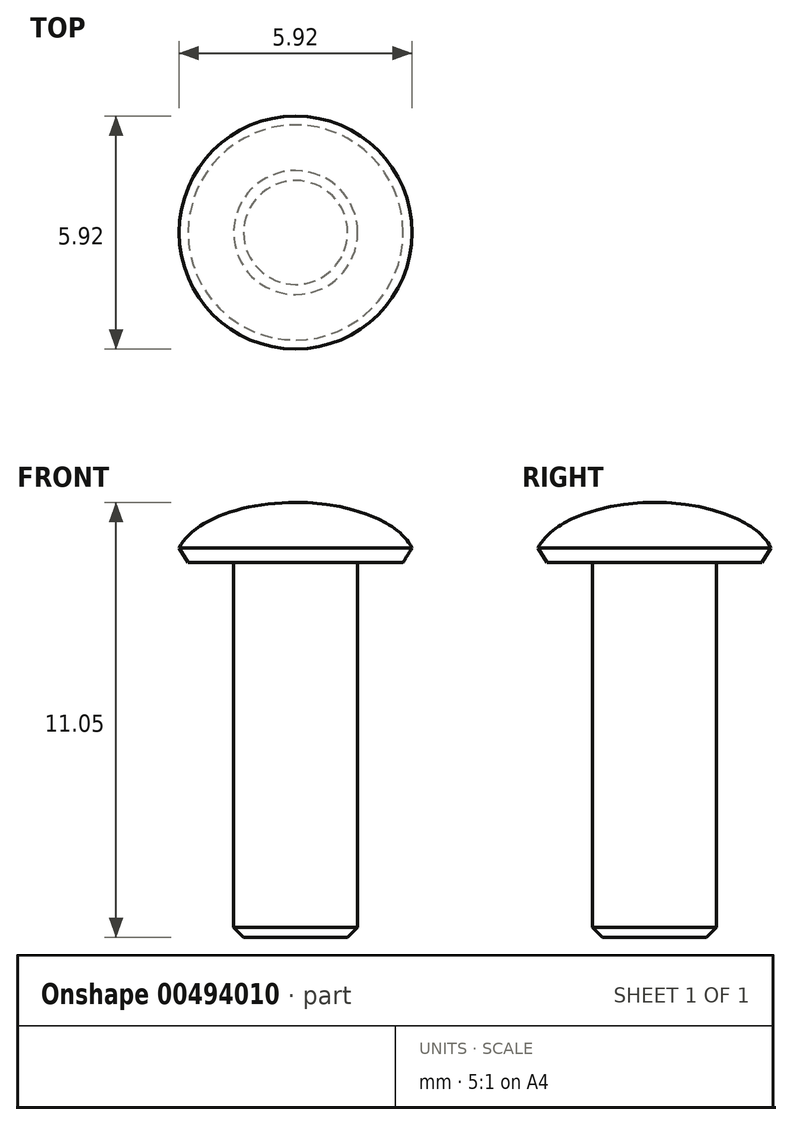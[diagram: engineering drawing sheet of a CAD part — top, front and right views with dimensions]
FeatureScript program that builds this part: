
annotation { "Feature Type Name" : "Feature", "Feature Type Description" : "" }
export const myFeature = defineFeature(function(context is Context, id is Id, definition is map)
    precondition{}
    {
        {
            var Q0;
            Q0=qCreatedBy(makeId("Front.planeOp"),FACE);
            var sketch = newSketch(context, id + "F0", { "sketchPlane" : qUnion([Q0])});
            skEllipticalArc(sketch, "E0", {});
            skLineSegment(sketch, "E1", {"start": v(0, 1.52) * mm, "end": v(0, 0) * mm});
            skLineSegment(sketch, "E2", {"start": v(0, 0) * mm, "end": v(0, -9.53) * mm});
            skLineSegment(sketch, "E3", {"start": v(0, -9.53) * mm, "end": v(-1.57, -9.53) * mm});
            skLineSegment(sketch, "E4", {"start": v(-1.57, -9.53) * mm, "end": v(-1.57, 0) * mm});
            skLineSegment(sketch, "E5", {"start": v(-1.57, 0) * mm, "end": v(-3.05, 0) * mm});
            const initialGuessF0  = {"E0": [0, 0, -1, 0, 0.003048, 0.001524, 4.71238898038469, 0]};
            skSetInitialGuess(sketch, initialGuessF0);
            skSolve(sketch);
        }
        {
            var Q0;
            Q0 = qSketchRegion(id + "F0", true);
            var Q1;
            Q1=sQuery(id+"F0.wireOp",EDGE,"E2");
            revolve(context, id + "F1", {"entities" : qUnion([Q0]), "axis" : qUnion([Q1]), "revolveType" : RevolveType.FULL});
        }
        {
            var Q0;
            Q0=makeQuery(id+"F1.opRevolve","SWEPT_EDGE",EDGE,{"disambiguationData":[OSD([sQuery(id+"F0.wireOp",EDGE,"E0"),sQuery(id+"F0.wireOp",EDGE,"E5")])]});
            var Q1;
            Q1=makeQuery(id+"F1.opRevolve","SWEPT_EDGE",EDGE,{"disambiguationData":[OSD([sQuery(id+"F0.wireOp",EDGE,"E3"),sQuery(id+"F0.wireOp",EDGE,"E4")])]});
            chamfer(context, id + "F2", {"entities" : qUnion([Q0, Q1]), "width" : 0.25 * mm, "tangentPropagation" : true});
        }
    });
